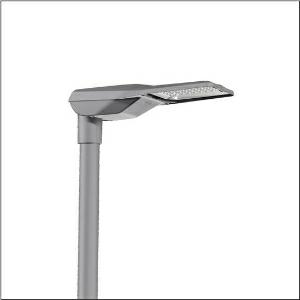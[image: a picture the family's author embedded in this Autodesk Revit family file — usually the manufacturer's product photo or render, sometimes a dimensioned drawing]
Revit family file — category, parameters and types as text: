
# Revit family: streetlight_sl_21_iq_mini___st1_0a_5xe2d61g08hb_24ab
name_source: partatom
category: Lighting Fixtures
units: mm (PartAtom-declared; Revit-internal decimal feet)

## family parameters
Cut with Voids When Loaded = No
Host = Face
Light Source = No
Part Type = Normal
Room Calculation Point = No
Round Connector Dimension = Use Diameter
Shared = No

## types (1)
- --- (1 x LED, 8480 lm, 70.9 W, 2700K)
    Apparent Load = 71 VA
    CIE Flux Codes = 37 72 97 100 100
    Color Rendering = 70
    Color Temperature = 2700K
    Default Elevation = 1800 mm
    Description = Streetlight SL 21 iQ mini, mast luminaire, primary light control with lens, of PMMA, primary optical cover: cover, of toughened safety glass, transparent, light distribution: ST1.0a, light emission: direct distribution, primary light characteristic: asymmetric, installation type: post-top, side-entry, LED, High Power LED, rated luminous flux: 8.480lm, luminous efficacy: 120lm/W, light colour: 727, colour temperature: 2700K, control gear: iQ Street-Remote, control: Street-Remote, Auto-Match, Temp-Guard, Lumen-Switch, Night-Set, Smart-Wire, Light-Fading, Desk-Remote (wireless, voltage-free reading and setting of iQ features in the workshop via application-optimized NFC function/RFID function), optimised constant luminous flux control (CLO 2.0), pre-setting: linear dimming characteristic, mains connection: 220..240V, AC, 50/60Hz, start of lifetime: 71W, end of service life: 75W, reduction: 31W, luminaire housing, of diecast aluminium, powder-coated, Siteco® metallic grey (DB 702S), corrosivity category C5 mid according to DIN EN ISO 12944, please order mast flange separately, inclination adjustable: 0°, 5°, 10°, 15°, sealing non-destructively replaceable, multi-level sealing system, length: 628mm, width: 235mm, height: 110mm, mast flange for spigot size: 42mm (side-entry): 5XC10008XM4, 60/48mm (side-entry/post-top): 5XC10108XM2, 76/60mm (side-entry/post-top): 5XC10108XM1, mounting height: 4..8m, protection rating (complete): IP66, insulation class (complete): insulation class II (safety insulation), certification: CE, ENEC, ENEC+, VDE, impact resistance: IK10, permissible operating ambient temperature for outdoor applications: -40..+50°C, standard-compliant lighting for roads and squares, packaging unit: 1 piece

Light Distribution: ST1.0a
    Height = 110 mm
    Lamp = 1 x LED
    Lamp Light Flux = 8480 lm
    Lamp Power = 70.9 W
    Lamp count = 1
    Length = 625 mm
    Luminous efficacy = 120 lm/W
    Manufacturer = Siteco
    ModVariant = No
    Model = 5XE2D61G08HB
    Number of Poles = 1
    OnlyDefault = Yes
    Power Factor = 1
    Product Name = Streetlight SL 21 iQ mini | ST1.0a
    Product group = mast luminaire | pylon top
    ProductGroupID = 6100
    Protection Class = Protection class II
    Protection Degree = IP 66
    RLX_Detail_Level = 1
    RLX_Emergency_Light_Flux = 0 lm
    RLX_Emergency_Type = 0
    RLX_Emergency_Type_DB = No
    RlxData = <blob elided: 26329 chars, md5=ef4d58c4>
    Socket = socket
    Standby Power = 0 W
    System Light Flux = 8480 lm
    System Power = 71 W
    Type Comments = factory setting: luminous flux: 100 % | dim-lin: 254 | 711 mA
    Type Image = l_1003519.jpg
    URL = http://relux.com
    VarID = @adj_158226
    Voltage = 0 V
    Weight = 0.00 kg
    Width = 234 mm

## geometry (parser evidence)
native form markers: Blend x4, Sweep x11
no freeform markers — native parametric forms only
